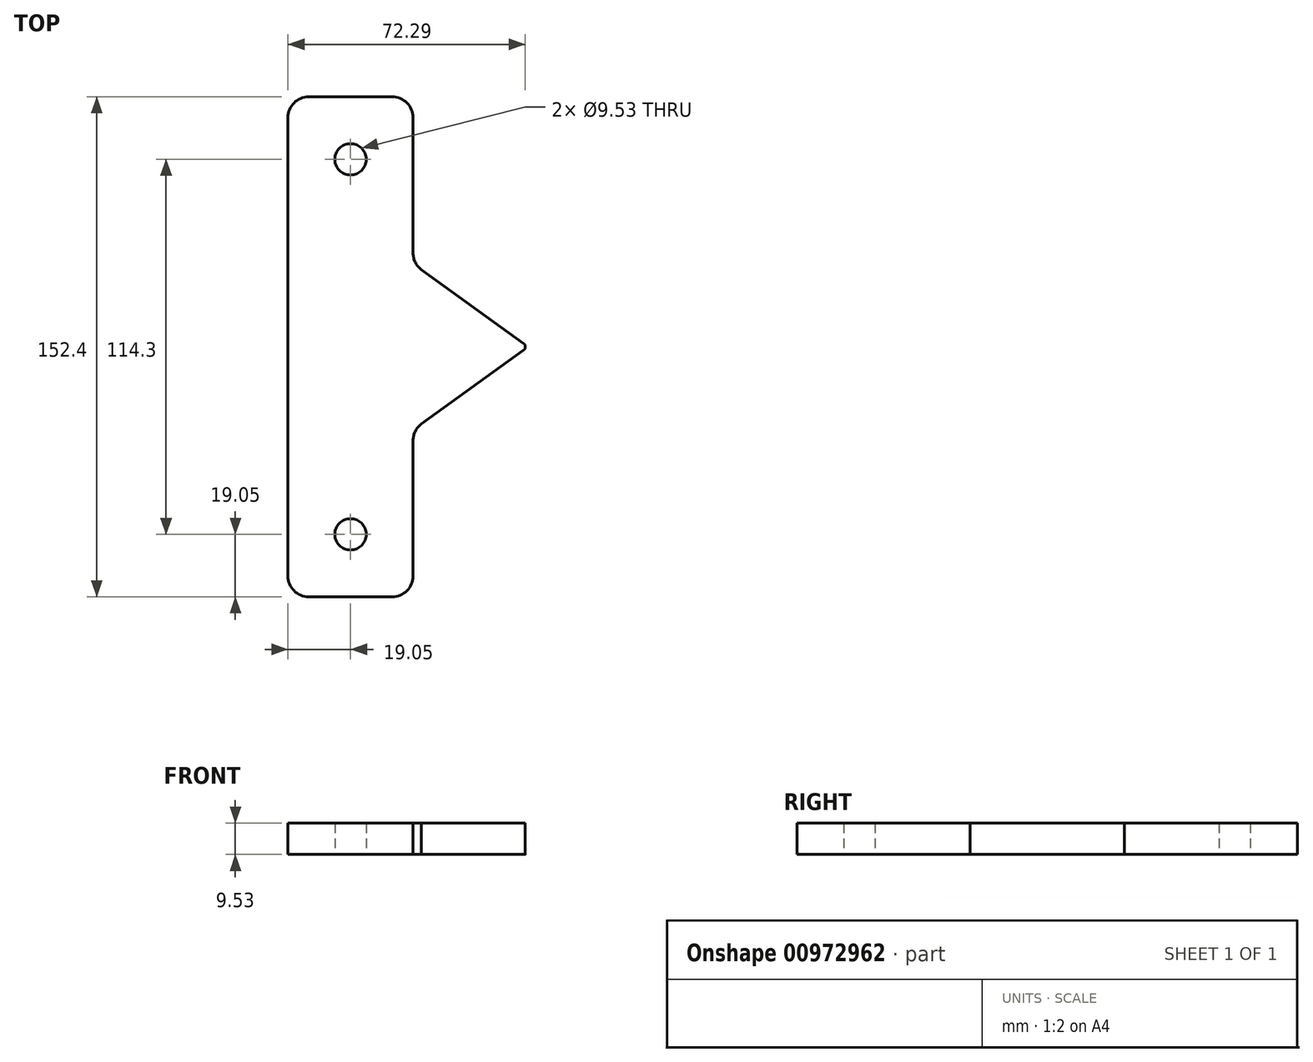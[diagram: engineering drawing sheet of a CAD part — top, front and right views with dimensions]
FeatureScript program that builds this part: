
annotation { "Feature Type Name" : "Feature", "Feature Type Description" : "" }
export const myFeature = defineFeature(function(context is Context, id is Id, definition is map)
    precondition{}
    {
        {
            var Q0;
            Q0=qCreatedBy(makeId("Top.planeOp"),FACE);
            var sketch = newSketch(context, id + "F0", { "sketchPlane" : qUnion([Q0])});
            skLineSegment(sketch, "E0.bottom", {"start": v(6.35, 0) * mm, "end": v(31.75, 0) * mm});
            skLineSegment(sketch, "E0.top", {"start": v(6.35, 152.4) * mm, "end": v(31.75, 152.4) * mm});
            skLineSegment(sketch, "E0.left", {"start": v(0, 6.35) * mm, "end": v(0, 146.05) * mm});
            skLineSegment(sketch, "E0.right", {"start": v(38.1, 104.8) * mm, "end": v(38.1, 146.05) * mm});
            skCircle(sketch, "E1", {"center": v(19.05, 133.35) * mm, "radius": 4.76 * mm});
            skCircle(sketch, "E2", {"center": v(19.05, 19.05) * mm, "radius": 4.76 * mm});
            skPoint(sketch, "E3.newPointA", {"position": v(38.1, 101.6) * mm});
            skArc(sketch, "E3.filletArc", {"start": v(38.1, 104.8) * mm, "mid": v(38.78, 101.94) * mm, "end": v(40.66, 99.7) * mm});
            skLineSegment(sketch, "E4", {"start": v(38.1, 47.6) * mm, "end": v(38.1, 6.35) * mm});
            skPoint(sketch, "E5.visualSharp", {"position": v(38.1, 50.8) * mm});
            skArc(sketch, "E5.filletArc", {"start": v(40.66, 52.7) * mm, "mid": v(38.78, 50.46) * mm, "end": v(38.1, 47.6) * mm});
            skLineSegment(sketch, "E6", {"start": v(40.66, 99.7) * mm, "end": v(71.76, 77.23) * mm});
            skLineSegment(sketch, "E7", {"start": v(40.66, 52.7) * mm, "end": v(71.76, 75.17) * mm});
            skArc(sketch, "E8.trimOffspring", {"start": v(71.76, 75.17) * mm, "mid": v(72.29, 76.2) * mm, "end": v(71.76, 77.23) * mm});
            skPoint(sketch, "E9.visualSharp", {"position": v(38.1, 152.4) * mm});
            skArc(sketch, "E9.filletArc", {"start": v(38.1, 146.05) * mm, "mid": v(36.24, 150.54) * mm, "end": v(31.75, 152.4) * mm});
            skPoint(sketch, "E10.visualSharp", {"position": v(0, 152.4) * mm});
            skArc(sketch, "E10.filletArc", {"start": v(6.35, 152.4) * mm, "mid": v(1.86, 150.54) * mm, "end": v(0, 146.05) * mm});
            skPoint(sketch, "E11.visualSharp", {"position": v(0, 0) * mm});
            skArc(sketch, "E11.filletArc", {"start": v(0, 6.35) * mm, "mid": v(1.86, 1.86) * mm, "end": v(6.35, 0) * mm});
            skPoint(sketch, "E12.visualSharp", {"position": v(38.1, 0) * mm});
            skArc(sketch, "E12.filletArc", {"start": v(31.75, 0) * mm, "mid": v(36.24, 1.86) * mm, "end": v(38.1, 6.35) * mm});
            skSolve(sketch);
        }
        {
            var Q0;
            Q0=makeQuery(id+"F0.imprint","IMPRINT",FACE,{"disambiguationData":[TD([[makeQuery(id+"F0.imprint","IMPRINT",EDGE,{"derivedFrom":sQuery(id+"F0.wireOp",EDGE,"E0.bottom")}),1.0]])]});
            extrude(context, id + "F1", {"entities" : qUnion([Q0]), "depth" : 9.52 * mm, "offsetDistance" : 25.4 * mm});
        }
    });
